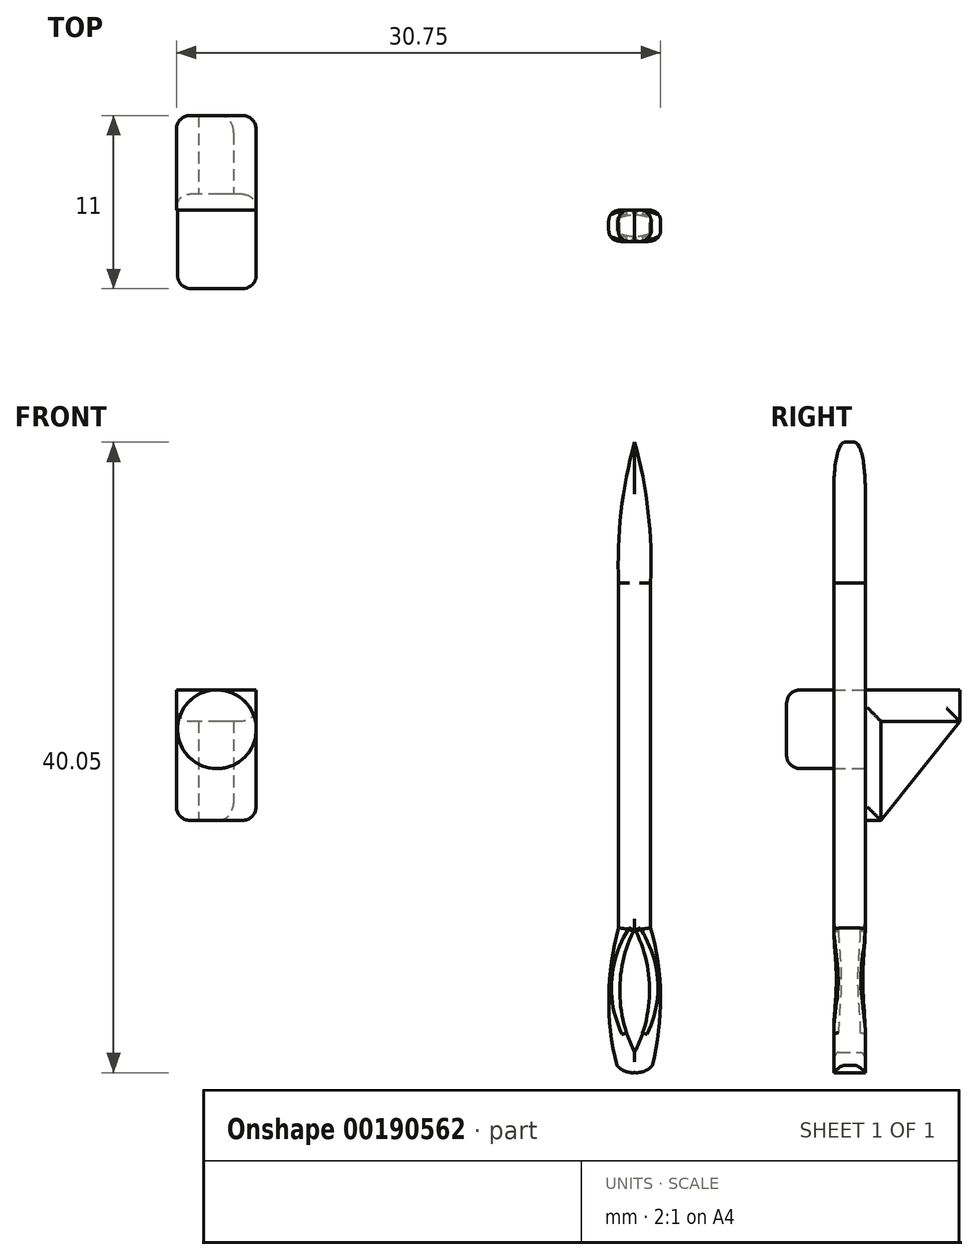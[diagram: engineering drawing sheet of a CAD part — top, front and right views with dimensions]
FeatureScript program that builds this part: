
annotation { "Feature Type Name" : "Feature", "Feature Type Description" : "" }
export const myFeature = defineFeature(function(context is Context, id is Id, definition is map)
    precondition{}
    {
        {
            var Q0;
            Q0=qCreatedBy(makeId("Front.planeOp"),FACE);
            var sketch = newSketch(context, id + "F0", { "sketchPlane" : qUnion([Q0])});
            skLineSegment(sketch, "E0", {"start": v(0, 18.24) * mm, "end": v(0, -12.66) * mm});
            skLineSegment(sketch, "E1", {"start": v(1.02, 9.1) * mm, "end": v(1.02, -12.61) * mm});
            skArc(sketch, "E2", {"start": v(1.02, 9.29) * mm, "mid": v(0.86, 13.8) * mm, "end": v(0, 18.24) * mm});
            skArc(sketch, "E3", {"start": v(0, -21.8) * mm, "mid": v(0.62, -21.72) * mm, "end": v(1.12, -21.35) * mm});
            skArc(sketch, "E4", {"start": v(1.12, -21.35) * mm, "mid": v(1.64, -16.97) * mm, "end": v(1.02, -12.61) * mm});
            skLineSegment(sketch, "E5", {"start": v(0, -20.51) * mm, "end": v(0, -21.8) * mm});
            skLineSegment(sketch, "E6", {"start": v(0, -12.66) * mm, "end": v(0, -20.51) * mm});
            skArc(sketch, "E7", {"start": v(0, -20.51) * mm, "mid": v(0.94, -16.59) * mm, "end": v(0, -12.66) * mm});
            skLineSegment(sketch, "E8.MirrorCS", {"start": v(-1.02, 9.1) * mm, "end": v(-1.02, -12.61) * mm});
            skArc(sketch, "E9.MirrorCS", {"start": v(0, -21.8) * mm, "mid": v(-0.62, -21.72) * mm, "end": v(-1.12, -21.35) * mm});
            skArc(sketch, "E10.MirrorCS", {"start": v(0, -20.51) * mm, "mid": v(-0.94, -16.59) * mm, "end": v(0, -12.66) * mm});
            skArc(sketch, "E11.MirrorCS", {"start": v(-1.12, -21.35) * mm, "mid": v(-1.64, -16.97) * mm, "end": v(-1.02, -12.61) * mm});
            skArc(sketch, "E12.MirrorCS", {"start": v(-1.02, 9.29) * mm, "mid": v(-0.86, 13.8) * mm, "end": v(0, 18.24) * mm});
            skLineSegment(sketch, "E13", {"start": v(1.02, 9.29) * mm, "end": v(1.02, 9.1) * mm});
            skLineSegment(sketch, "E14", {"start": v(-1.02, 9.29) * mm, "end": v(-1.02, 9.1) * mm});
            skSolve(sketch);
        }
        {
            var Q0;
            Q0=makeQuery(id+"F0.imprint","IMPRINT",FACE,{"disambiguationData":[TD([[makeQuery(id+"F0.imprint","IMPRINT",EDGE,{"derivedFrom":sQuery(id+"F0.wireOp",EDGE,"E0")}),-1.0]])]});
            var Q1;
            Q1=makeQuery(id+"F0.imprint","IMPRINT",FACE,{"disambiguationData":[TD([[makeQuery(id+"F0.imprint","IMPRINT",EDGE,{"derivedFrom":sQuery(id+"F0.wireOp",EDGE,"E0")}),1.0]])]});
            extrude(context, id + "F1", {"entities" : qUnion([Q0, Q1]), "depth" : 2 * mm});
        }
        {
            var Q0;
            Q0=makeQuery(id+"F1.opExtrude","CAP_EDGE",EDGE,{"disambiguationData":[OSD([sQuery(id+"F0.wireOp",EDGE,"E8.MirrorCS"),sQuery(id+"F0.wireOp",EDGE,"E14")])],"isStart":false});
            var Q1;
            Q1=makeQuery(id+"F1.opExtrude","CAP_EDGE",EDGE,{"disambiguationData":[OSD([sQuery(id+"F0.wireOp",EDGE,"E12.MirrorCS")])],"isStart":false});
            var Q2;
            Q2=makeQuery(id+"F1.opExtrude","CAP_EDGE",EDGE,{"disambiguationData":[OSD([sQuery(id+"F0.wireOp",EDGE,"E1"),sQuery(id+"F0.wireOp",EDGE,"E13")])],"isStart":false});
            var Q3;
            Q3=makeQuery(id+"F1.opExtrude","CAP_EDGE",EDGE,{"disambiguationData":[OSD([sQuery(id+"F0.wireOp",EDGE,"E2")])],"isStart":false});
            var Q4;
            Q4=makeQuery(id+"F1.opExtrude","CAP_EDGE",EDGE,{"disambiguationData":[OSD([sQuery(id+"F0.wireOp",EDGE,"E11.MirrorCS")])],"isStart":false});
            var Q5;
            Q5=makeQuery(id+"F1.opExtrude","CAP_EDGE",EDGE,{"disambiguationData":[OSD([sQuery(id+"F0.wireOp",EDGE,"E4")])],"isStart":false});
            var Q6;
            Q6=makeQuery(id+"F1.opExtrude","CAP_EDGE",EDGE,{"disambiguationData":[OSD([sQuery(id+"F0.wireOp",EDGE,"E8.MirrorCS"),sQuery(id+"F0.wireOp",EDGE,"E14")])],"isStart":true});
            var Q7;
            Q7=makeQuery(id+"F1.opExtrude","CAP_EDGE",EDGE,{"disambiguationData":[OSD([sQuery(id+"F0.wireOp",EDGE,"E11.MirrorCS")])],"isStart":true});
            var Q8;
            Q8=makeQuery(id+"F1.opExtrude","CAP_EDGE",EDGE,{"disambiguationData":[OSD([sQuery(id+"F0.wireOp",EDGE,"E4")])],"isStart":true});
            var Q9;
            Q9=makeQuery(id+"F1.opExtrude","CAP_EDGE",EDGE,{"disambiguationData":[OSD([sQuery(id+"F0.wireOp",EDGE,"E1"),sQuery(id+"F0.wireOp",EDGE,"E13")])],"isStart":true});
            var Q10;
            Q10=makeQuery(id+"F1.opExtrude","CAP_EDGE",EDGE,{"disambiguationData":[OSD([sQuery(id+"F0.wireOp",EDGE,"E2")])],"isStart":true});
            var Q11;
            Q11=makeQuery(id+"F1.opExtrude","CAP_EDGE",EDGE,{"disambiguationData":[OSD([sQuery(id+"F0.wireOp",EDGE,"E12.MirrorCS")])],"isStart":true});
            fillet(context, id + "F2", {"entities" : qUnion([Q0, Q1, Q2, Q3, Q4, Q5, Q6, Q7, Q8, Q9, Q10, Q11]), "radius" : 0.7 * mm, "tangentPropagation" : true, "allowEdgeOverflow" : false});
        }
        {
            var Q0;
            Q0=makeQuery(id+"F2.opFillet","BLEND_EDGE",EDGE,{"blendedFrom":[makeQuery(id+"F1.opExtrude","CAP_EDGE",EDGE,{"disambiguationData":[OSD([sQuery(id+"F0.wireOp",EDGE,"E4")])],"isStart":true}),makeQuery(id+"F1.opExtrude","SWEPT_FACE",FACE,{"disambiguationData":[OSD([sQuery(id+"F0.wireOp",EDGE,"E7")])]})],"blendedInto":[makeQuery(id+"F1.opExtrude","SWEPT_FACE",FACE,{"disambiguationData":[OSD([sQuery(id+"F0.wireOp",EDGE,"E7")])]})]});
            var Q1;
            Q1=makeQuery(id+"F2.opFillet","BLEND_EDGE",EDGE,{"blendedFrom":[makeQuery(id+"F1.opExtrude","CAP_EDGE",EDGE,{"disambiguationData":[OSD([sQuery(id+"F0.wireOp",EDGE,"E11.MirrorCS")])],"isStart":true}),makeQuery(id+"F1.opExtrude","SWEPT_FACE",FACE,{"disambiguationData":[OSD([sQuery(id+"F0.wireOp",EDGE,"E10.MirrorCS")])]})],"blendedInto":[makeQuery(id+"F1.opExtrude","SWEPT_FACE",FACE,{"disambiguationData":[OSD([sQuery(id+"F0.wireOp",EDGE,"E10.MirrorCS")])]})]});
            var Q2;
            Q2=makeQuery(id+"F2.opFillet","BLEND_EDGE",EDGE,{"blendedFrom":[makeQuery(id+"F1.opExtrude","CAP_EDGE",EDGE,{"disambiguationData":[OSD([sQuery(id+"F0.wireOp",EDGE,"E11.MirrorCS")])],"isStart":false}),makeQuery(id+"F1.opExtrude","SWEPT_FACE",FACE,{"disambiguationData":[OSD([sQuery(id+"F0.wireOp",EDGE,"E10.MirrorCS")])]})],"blendedInto":[makeQuery(id+"F1.opExtrude","SWEPT_FACE",FACE,{"disambiguationData":[OSD([sQuery(id+"F0.wireOp",EDGE,"E10.MirrorCS")])]})]});
            var Q3;
            Q3=makeQuery(id+"F2.opFillet","BLEND_EDGE",EDGE,{"blendedFrom":[makeQuery(id+"F1.opExtrude","CAP_EDGE",EDGE,{"disambiguationData":[OSD([sQuery(id+"F0.wireOp",EDGE,"E4")])],"isStart":false}),makeQuery(id+"F1.opExtrude","SWEPT_FACE",FACE,{"disambiguationData":[OSD([sQuery(id+"F0.wireOp",EDGE,"E7")])]})],"blendedInto":[makeQuery(id+"F1.opExtrude","SWEPT_FACE",FACE,{"disambiguationData":[OSD([sQuery(id+"F0.wireOp",EDGE,"E7")])]})]});
            var Q4;
            Q4=makeQuery(id+"F1.opExtrude","CAP_EDGE",EDGE,{"disambiguationData":[OSD([sQuery(id+"F0.wireOp",EDGE,"E7")])],"isStart":false});
            var Q5;
            Q5=makeQuery(id+"F1.opExtrude","CAP_EDGE",EDGE,{"disambiguationData":[OSD([sQuery(id+"F0.wireOp",EDGE,"E10.MirrorCS")])],"isStart":false});
            var Q6;
            Q6=makeQuery(id+"F1.opExtrude","CAP_EDGE",EDGE,{"disambiguationData":[OSD([sQuery(id+"F0.wireOp",EDGE,"E7")])],"isStart":true});
            var Q7;
            Q7=makeQuery(id+"F1.opExtrude","CAP_EDGE",EDGE,{"disambiguationData":[OSD([sQuery(id+"F0.wireOp",EDGE,"E10.MirrorCS")])],"isStart":true});
            fillet(context, id + "F3", {"entities" : qUnion([Q0, Q1, Q2, Q3, Q4, Q5, Q6, Q7]), "radius" : 0.3 * mm, "tangentPropagation" : true, "allowEdgeOverflow" : false});
        }
        {
            var Q0;
            Q0=qCreatedBy(makeId("Front.planeOp"),FACE);
            var sketch = newSketch(context, id + "F4", { "sketchPlane" : qUnion([Q0])});
            skCircle(sketch, "E15", {"center": v(-26.53, 0) * mm, "radius": 2.5 * mm});
            skSolve(sketch);
        }
        {
            var Q0;
            Q0=makeQuery(id+"F4.imprint","IMPRINT",FACE,{"disambiguationData":[TD([[makeQuery(id+"F4.imprint","IMPRINT",EDGE,{"derivedFrom":sQuery(id+"F4.wireOp",EDGE,"E15")}),1.0]])]});
            extrude(context, id + "F5", {"entities" : qUnion([Q0]), "depth" : 5 * mm});
        }
        {
            var Q0;
            Q0=makeQuery(id+"F5.opExtrude","CAP_FACE",FACE,{"disambiguationData":[OSD([sQuery(id+"F4.wireOp",EDGE,"E15")])],"isStart":true});
            var sketch = newSketch(context, id + "F6", { "sketchPlane" : qUnion([Q0])});
            skLineSegment(sketch, "E16.bottom", {"start": v(24.05, 2.51) * mm, "end": v(29.1, 2.51) * mm});
            skLineSegment(sketch, "E16.top", {"start": v(24.05, -5.79) * mm, "end": v(29.1, -5.79) * mm});
            skLineSegment(sketch, "E16.left", {"start": v(24.05, 2.51) * mm, "end": v(24.05, -5.79) * mm});
            skLineSegment(sketch, "E16.right", {"start": v(29.1, 2.51) * mm, "end": v(29.1, -5.79) * mm});
            skSolve(sketch);
        }
        {
            var Q0;
            {var subQ4=sQuery(id+"F6.wireOp",EDGE,"E16.bottom");Q0=makeQuery(id+"F6.imprint","IMPRINT",FACE,{"disambiguationData":[TD([[makeQuery(id+"F6.imprint","IMPRINT",EDGE,{"derivedFrom":subQ4}),-1.0]])]});}
            var Q1;
            {var subQ0=sQuery(id+"F6.wireOp",EDGE,"E16.left");var subQ1=makeQuery(id+"F5.opExtrude","CAP_EDGE",EDGE,{"disambiguationData":[OSD([sQuery(id+"F4.wireOp",EDGE,"E15")])],"isStart":true});var subQ2=makeQuery(id+"F6.imprint","INTERSECT",VERTEX,{"disambiguationData":[OD(0.0)],"derivedFrom":[subQ1,subQ0]});Q1=makeQuery(id+"F6.imprint","IMPRINT",FACE,{"disambiguationData":[TD([[makeQuery(id+"F6.imprint","IMPRINT",EDGE,{"disambiguationData":[TD([[subQ2,-1.0]])],"derivedFrom":subQ0}),1.0]])]});}
            extrude(context, id + "F7", {"entities" : qUnion([Q0, Q1]), "operationType" : NewBodyOperationType.ADD, "depth" : 1 * mm});
        }
        {
            var Q0;
            Q0=makeQuery(id+"F7.opExtrude","CAP_FACE",FACE,{"disambiguationData":[OSD([sQuery(id+"F6.wireOp",EDGE,"E16.bottom"),sQuery(id+"F6.wireOp",EDGE,"E16.top"),sQuery(id+"F6.wireOp",EDGE,"E16.left"),sQuery(id+"F6.wireOp",EDGE,"E16.right")])],"isStart":false});
            var sketch = newSketch(context, id + "F8", { "sketchPlane" : qUnion([Q0])});
            skLineSegment(sketch, "E17.bottom", {"start": v(24.05, 2.51) * mm, "end": v(29.1, 2.51) * mm});
            skLineSegment(sketch, "E17.top", {"start": v(24.05, 0.51) * mm, "end": v(29.1, 0.51) * mm});
            skLineSegment(sketch, "E17.left", {"start": v(24.05, 2.51) * mm, "end": v(24.05, 0.51) * mm});
            skLineSegment(sketch, "E17.right", {"start": v(29.1, 2.51) * mm, "end": v(29.1, 0.51) * mm});
            skLineSegment(sketch, "E18", {"start": v(26.57, 0.51) * mm, "end": v(26.57, -5.79) * mm});
            skLineSegment(sketch, "E19", {"start": v(25.47, 0.51) * mm, "end": v(25.47, -5.79) * mm});
            skLineSegment(sketch, "E20", {"start": v(25.47, -5.79) * mm, "end": v(26.57, -5.79) * mm});
            skLineSegment(sketch, "E21.MirrorCS", {"start": v(27.68, 0.51) * mm, "end": v(27.68, -5.79) * mm});
            skLineSegment(sketch, "E22.MirrorCS", {"start": v(27.68, -5.79) * mm, "end": v(26.57, -5.79) * mm});
            skSolve(sketch);
        }
        {
            var Q0;
            Q0=makeQuery(id+"F8.imprint","IMPRINT",FACE,{"disambiguationData":[TD([[makeQuery(id+"F8.imprint","IMPRINT",EDGE,{"derivedFrom":sQuery(id+"F8.wireOp",EDGE,"E17.bottom")}),-1.0]])]});
            var Q1;
            {var subQ0=sQuery(id+"F8.wireOp",EDGE,"E18");Q1=makeQuery(id+"F8.imprint","IMPRINT",FACE,{"disambiguationData":[TD([[makeQuery(id+"F8.imprint","IMPRINT",EDGE,{"derivedFrom":subQ0}),1.0]])]});}
            var Q2;
            {var subQ0=sQuery(id+"F8.wireOp",EDGE,"E18");Q2=makeQuery(id+"F8.imprint","IMPRINT",FACE,{"disambiguationData":[TD([[makeQuery(id+"F8.imprint","IMPRINT",EDGE,{"derivedFrom":subQ0}),-1.0]])]});}
            extrude(context, id + "F9", {"entities" : qUnion([Q0, Q1, Q2]), "operationType" : NewBodyOperationType.ADD, "depth" : 5 * mm});
        }
        {
            var Q0;
            Q0=makeQuery(id+"F9.opExtrude","SWEPT_FACE",FACE,{"disambiguationData":[OSD([sQuery(id+"F8.wireOp",EDGE,"E21.MirrorCS")])]});
            var sketch = newSketch(context, id + "F10", { "sketchPlane" : qUnion([Q0])});
            skLineSegment(sketch, "E23", {"start": v(-6, 0.51) * mm, "end": v(-1, -5.79) * mm});
            skLineSegment(sketch, "E24", {"start": v(-1, -5.79) * mm, "end": v(-6, -5.79) * mm});
            skLineSegment(sketch, "E25", {"start": v(-6, -5.79) * mm, "end": v(-6, 0.51) * mm});
            skSolve(sketch);
        }
        {
            var Q0;
            Q0=makeQuery(id+"F10.imprint","IMPRINT",FACE,{"disambiguationData":[TD([[makeQuery(id+"F10.imprint","IMPRINT",EDGE,{"derivedFrom":sQuery(id+"F10.wireOp",EDGE,"E23")}),-1.0]])]});
            extrude(context, id + "F11", {"entities" : qUnion([Q0]), "operationType" : NewBodyOperationType.REMOVE, "oppositeDirection" : true, "depth" : 25.4 * mm});
        }
        {
            var Q0;
            Q0=makeQuery(id+"F5.opExtrude","CAP_EDGE",EDGE,{"disambiguationData":[OSD([sQuery(id+"F4.wireOp",EDGE,"E15")])],"isStart":false});
            var Q1;
            Q1=makeQuery(id+"F9.opExtrude","CAP_EDGE",EDGE,{"disambiguationData":[OSD([sQuery(id+"F8.wireOp",EDGE,"E17.left")])],"isStart":false});
            var Q2;
            Q2=makeQuery(id+"F7.opExtrude","SWEPT_EDGE",EDGE,{"disambiguationData":[OSD([sQuery(id+"F6.wireOp",EDGE,"E16.top"),sQuery(id+"F6.wireOp",EDGE,"E16.left")])]});
            var Q3;
            Q3=makeQuery(id+"F9.opExtrude","CAP_EDGE",EDGE,{"disambiguationData":[OSD([sQuery(id+"F8.wireOp",EDGE,"E17.right")])],"isStart":false});
            var Q4;
            Q4=makeQuery(id+"F7.opExtrude","SWEPT_EDGE",EDGE,{"disambiguationData":[OSD([sQuery(id+"F6.wireOp",EDGE,"E16.top"),sQuery(id+"F6.wireOp",EDGE,"E16.right")])]});
            var Q5;
            Q5=makeQuery(id+"F11.boolean.opBoolean","COPY",EDGE,{"derivedFrom":makeQuery(id+"F11.opExtrude","CAP_EDGE",EDGE,{"disambiguationData":[OSD([sQuery(id+"F10.wireOp",EDGE,"E23")])],"isStart":true})});
            var Q6;
            Q6=makeQuery(id+"F11.boolean.opBoolean","INTERSECT",EDGE,{"derivedFrom":[makeQuery(id+"F9.opExtrude","SWEPT_FACE",FACE,{"disambiguationData":[OSD([sQuery(id+"F8.wireOp",EDGE,"E19")])]}),makeQuery(id+"F11.opExtrude","SWEPT_FACE",FACE,{"disambiguationData":[OSD([sQuery(id+"F10.wireOp",EDGE,"E23")])]})]});
            var Q7;
            Q7=makeQuery(id+"F9.opExtrude","SWEPT_EDGE",EDGE,{"disambiguationData":[OSD([sQuery(id+"F6.wireOp",EDGE,"E16.right"),sQuery(id+"F8.wireOp",EDGE,"E17.top"),sQuery(id+"F8.wireOp",EDGE,"E17.right")])]});
            var Q8;
            Q8=makeQuery(id+"F7.opExtrude","CAP_EDGE",EDGE,{"disambiguationData":[OSD([sQuery(id+"F6.wireOp",EDGE,"E16.right")])],"isStart":false});
            var Q9;
            Q9=makeQuery(id+"F7.opExtrude","CAP_EDGE",EDGE,{"disambiguationData":[OSD([sQuery(id+"F6.wireOp",EDGE,"E16.left")])],"isStart":false});
            var Q10;
            Q10=makeQuery(id+"F9.opExtrude","SWEPT_EDGE",EDGE,{"disambiguationData":[OSD([sQuery(id+"F6.wireOp",EDGE,"E16.left"),sQuery(id+"F8.wireOp",EDGE,"E17.top"),sQuery(id+"F8.wireOp",EDGE,"E17.left")])]});
            fillet(context, id + "F12", {"entities" : qUnion([Q0, Q1, Q2, Q3, Q4, Q5, Q6, Q7, Q8, Q9, Q10]), "radius" : 0.86 * mm, "tangentPropagation" : true, "allowEdgeOverflow" : false});
        }
    });
